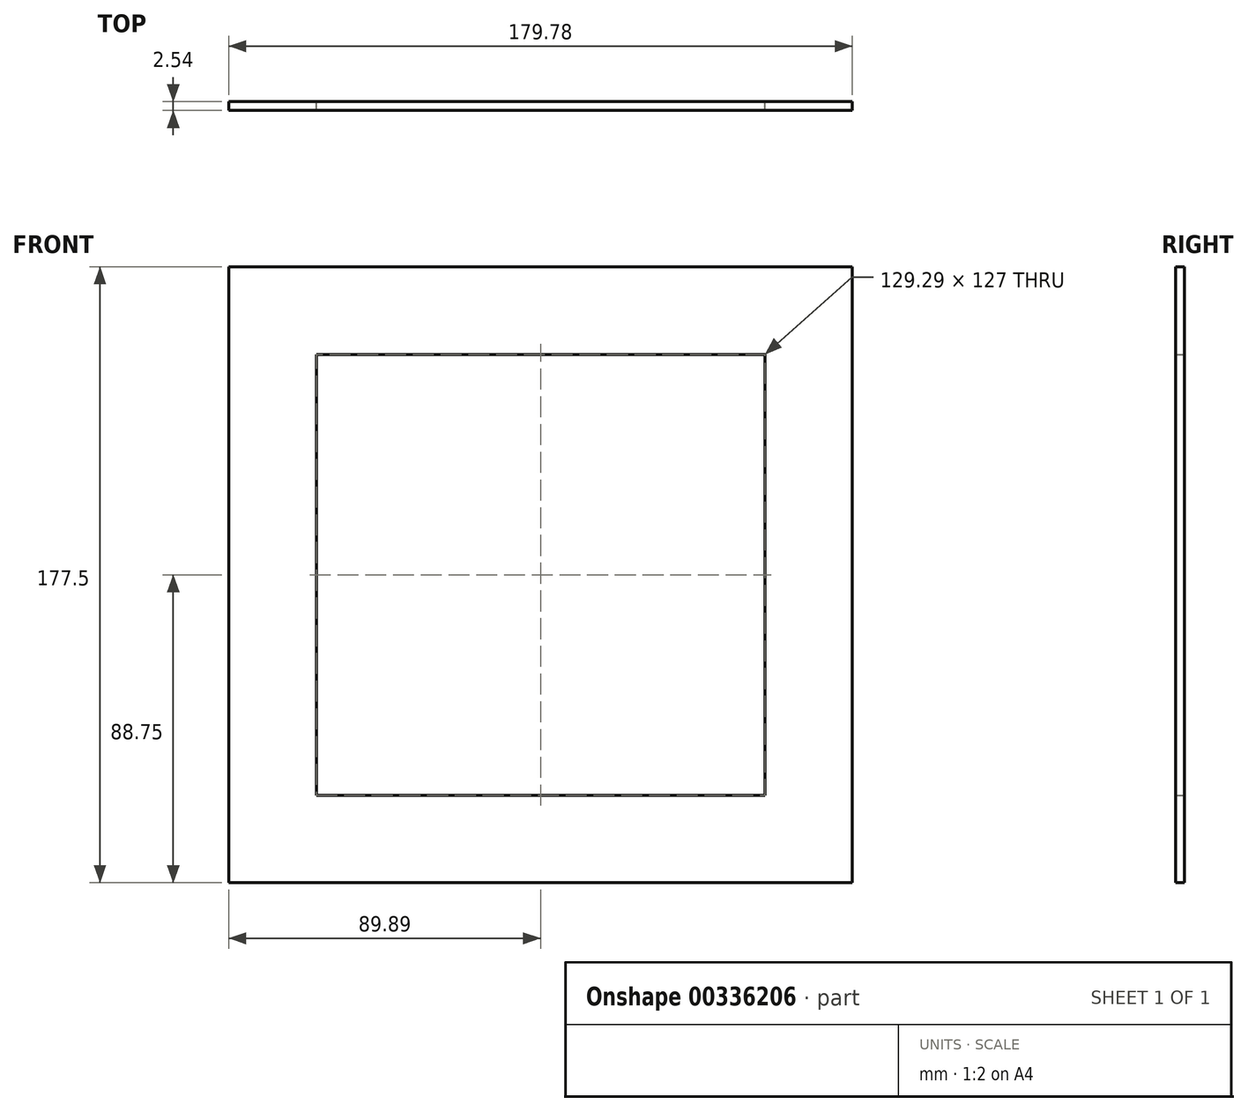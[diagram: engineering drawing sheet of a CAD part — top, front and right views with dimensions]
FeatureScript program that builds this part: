
annotation { "Feature Type Name" : "Feature", "Feature Type Description" : "" }
export const myFeature = defineFeature(function(context is Context, id is Id, definition is map)
    precondition{}
    {
        {
            var Q0;
            Q0=qCreatedBy(makeId("Front.planeOp"),FACE);
            var sketch = newSketch(context, id + "F0", { "sketchPlane" : qUnion([Q0])});
            skLineSegment(sketch, "E0.bottom", {"start": v(-89.9, 88.75) * mm, "end": v(89.9, 88.75) * mm});
            skLineSegment(sketch, "E0.top", {"start": v(-89.9, -88.75) * mm, "end": v(89.9, -88.75) * mm});
            skLineSegment(sketch, "E0.left", {"start": v(-89.9, 88.75) * mm, "end": v(-89.9, -88.75) * mm});
            skLineSegment(sketch, "E0.right", {"start": v(89.9, 88.75) * mm, "end": v(89.9, -88.75) * mm});
            skPoint(sketch, "E0.middle", {"position": v(0, 0) * mm});
            skLineSegment(sketch, "E1.bottom", {"start": v(-64.64, 63.5) * mm, "end": v(64.64, 63.5) * mm});
            skLineSegment(sketch, "E1.top", {"start": v(-64.64, -63.5) * mm, "end": v(64.64, -63.5) * mm});
            skLineSegment(sketch, "E1.left", {"start": v(-64.64, 63.5) * mm, "end": v(-64.64, -63.5) * mm});
            skLineSegment(sketch, "E1.right", {"start": v(64.64, 63.5) * mm, "end": v(64.64, -63.5) * mm});
            skSolve(sketch);
        }
        {
            var Q0;
            Q0=makeQuery(id+"F0.imprint","IMPRINT",FACE,{"disambiguationData":[TD([[makeQuery(id+"F0.imprint","IMPRINT",EDGE,{"derivedFrom":sQuery(id+"F0.wireOp",EDGE,"E0.bottom")}),-1.0]])]});
            extrude(context, id + "F1", {"entities" : qUnion([Q0]), "endBound" : BoundingType.SYMMETRIC, "depth" : 2.54 * mm});
        }
    });
